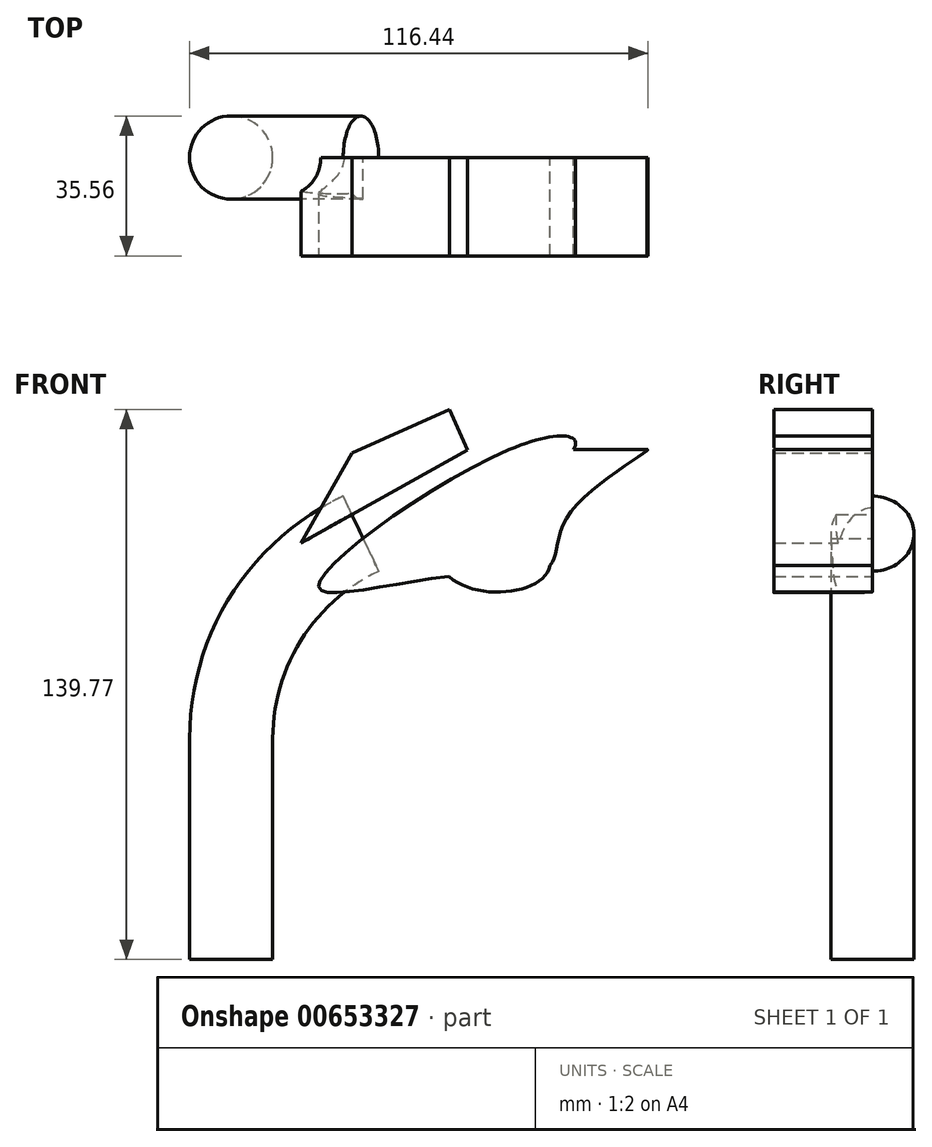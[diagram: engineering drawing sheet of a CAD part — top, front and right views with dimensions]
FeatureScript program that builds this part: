
annotation { "Feature Type Name" : "Feature", "Feature Type Description" : "" }
export const myFeature = defineFeature(function(context is Context, id is Id, definition is map)
    precondition{}
    {
        {
            var Q0;
            Q0=qCreatedBy(makeId("Top.planeOp"),FACE);
            var sketch = newSketch(context, id + "F0", { "sketchPlane" : qUnion([Q0])});
            skCircle(sketch, "E0", {"center": v(0, 0) * mm, "radius": 10.56 * mm});
            skSolve(sketch);
        }
        {
            var Q0;
            Q0=qCreatedBy(makeId("Front.planeOp"),FACE);
            var sketch = newSketch(context, id + "F1", { "sketchPlane" : qUnion([Q0])});
            skLineSegment(sketch, "E1", {"start": v(0, 0) * mm, "end": v(0, 56.18) * mm});
            skArc(sketch, "E2", {"start": v(32.97, 108.19) * mm, "mid": v(8.94, 86.97) * mm, "end": v(0, 56.18) * mm});
            skSolve(sketch);
        }
        {
            var Q0;
            Q0=makeQuery(id+"F0.imprint","IMPRINT",FACE,{"disambiguationData":[TD([[makeQuery(id+"F0.imprint","IMPRINT",EDGE,{"derivedFrom":sQuery(id+"F0.wireOp",EDGE,"E0")}),1.0]])]});
            var Q1;
            Q1=sQuery(id+"F1.wireOp",EDGE,"E2");
            var Q2;
            Q2=sQuery(id+"F1.wireOp",EDGE,"E1");
            sweep(context, id + "F2", {"profiles" : qUnion([Q0]), "path" : qUnion([Q1, Q2])});
        }
        {
            var Q0;
            Q0=qCreatedBy(makeId("Front.planeOp"),FACE);
            var sketch = newSketch(context, id + "F3", { "sketchPlane" : qUnion([Q0])});
            skLineSegment(sketch, "E3", {"start": v(17.75, 105.84) * mm, "end": v(30.72, 128.74) * mm});
            skLineSegment(sketch, "E4", {"start": v(30.72, 128.74) * mm, "end": v(55.5, 139.77) * mm});
            skLineSegment(sketch, "E5", {"start": v(55.5, 139.77) * mm, "end": v(60.05, 129.52) * mm});
            skLineSegment(sketch, "E6", {"start": v(60.05, 129.52) * mm, "end": v(17.75, 105.84) * mm});
            skFitSpline(sketch, "E7", {"points": [v(22.24, 94.8) * mm, v(74.85, 131.18) * mm, v(87.3, 130.24) * mm, v(78.44, 119.48) * mm, v(105.69, 129.6) * mm, v(86.3, 113.72) * mm, v(81.04, 100.13) * mm, v(55.37, 97.3) * mm, v(22.24, 94.8) * mm]});
            skFitSpline(sketch, "E8", {"points": [v(56.87, 119.2) * mm, v(81.04, 100.13) * mm, v(55.37, 97.3) * mm, v(56.87, 119.2) * mm]});
            skLineSegment(sketch, "E9", {"start": v(105.69, 129.6) * mm, "end": v(60.05, 129.52) * mm});
            skSolve(sketch);
        }
        {
            var Q0;
            Q0=makeQuery(id+"F3.imprint","IMPRINT",FACE,{"disambiguationData":[TD([[makeQuery(id+"F3.imprint","IMPRINT",EDGE,{"derivedFrom":sQuery(id+"F3.wireOp",EDGE,"E3")}),-1.0]])]});
            extrude(context, id + "F4", {"entities" : qUnion([Q0]), "operationType" : NewBodyOperationType.ADD, "depth" : 17.4 * mm, "offsetDistance" : 25 * mm});
        }
        {
            var Q0;
            Q0 = qSketchRegion(id + "F3", true);
            extrude(context, id + "F5", {"entities" : qUnion([Q0]), "operationType" : NewBodyOperationType.ADD, "depth" : 25 * mm, "offsetDistance" : 25 * mm});
        }
    });
